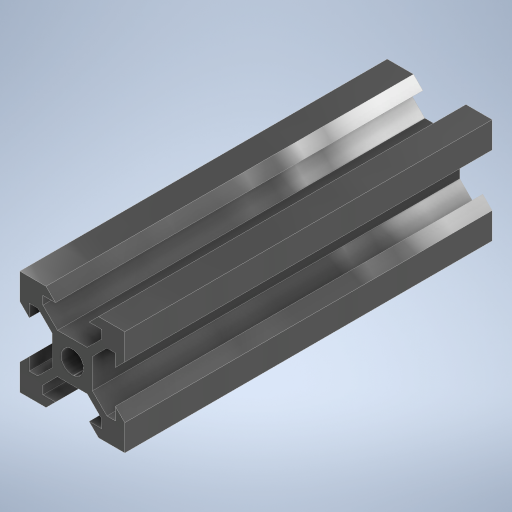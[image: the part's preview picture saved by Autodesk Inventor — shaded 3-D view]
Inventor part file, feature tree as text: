
AUTODESK INVENTOR PART (.ipt)
format: ipt  version: 2024.2 (Build 282272000, 272)  size: 318,976 bytes
history: native  units: mm
features: extrude x1, sketch x1
ambient origin geometry x8: Origin, YZ Plane, XZ Plane, XY Plane, X Axis, Y Axis, Z Axis, Center Point
bodies: Solid1 (feature_tree)
feature tree (2):
  extrude  "Extrusion1"  Depth=70.0mm
  sketch  "Sketch1"  dims[d16=10.0mm d19=3.2mm d21=4.4mm d22=4.4mm d24=45.0deg d25=1.8mm d27=1.8mm d28=45.0deg d29=3.2mm d31=1.4mm d33=2.15mm d34=3.825mm d35=3.825mm d36=135.0deg d37=40.0mm d39=360.0deg d41=70.0mm d42=0.0mm]
